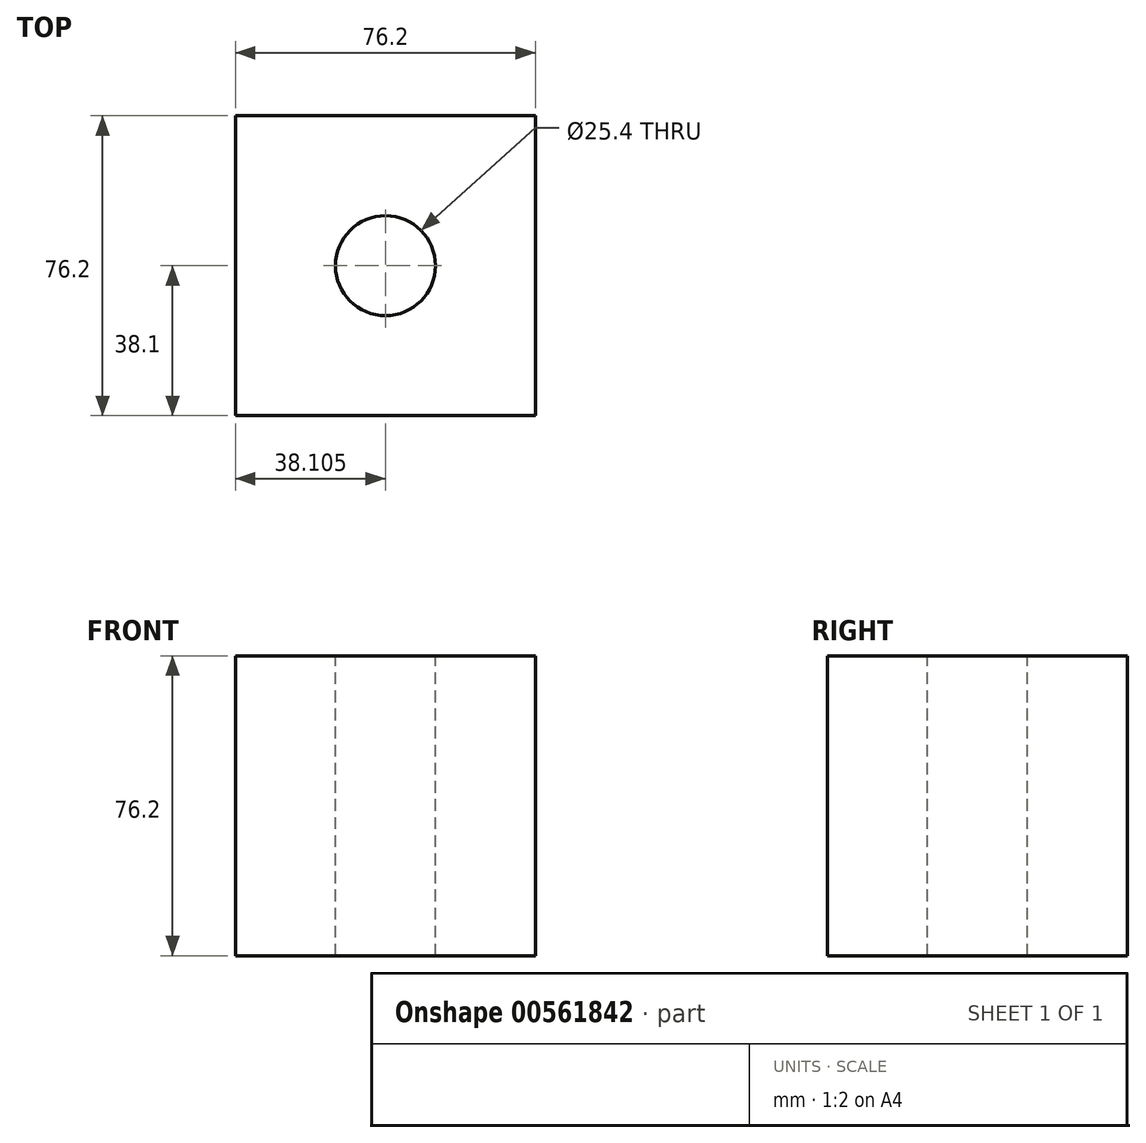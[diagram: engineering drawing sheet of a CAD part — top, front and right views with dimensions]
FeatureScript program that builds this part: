
annotation { "Feature Type Name" : "Feature", "Feature Type Description" : "" }
export const myFeature = defineFeature(function(context is Context, id is Id, definition is map)
    precondition{}
    {
        {
            var Q0;
            Q0=qCreatedBy(makeId("Front.planeOp"),FACE);
            var sketch = newSketch(context, id + "F0", { "sketchPlane" : qUnion([Q0])});
            skLineSegment(sketch, "E0.bottom", {"start": v(-44.93, 63.44) * mm, "end": v(31.27, 63.44) * mm});
            skLineSegment(sketch, "E0.top", {"start": v(-44.93, -12.76) * mm, "end": v(31.27, -12.76) * mm});
            skLineSegment(sketch, "E0.left", {"start": v(-44.93, 63.44) * mm, "end": v(-44.93, -12.76) * mm});
            skLineSegment(sketch, "E0.right", {"start": v(31.27, 63.44) * mm, "end": v(31.27, -12.76) * mm});
            skSolve(sketch);
        }
        {
            var Q0;
            Q0=makeQuery(id+"F0.imprint","IMPRINT",FACE,{"disambiguationData":[TD([[makeQuery(id+"F0.imprint","IMPRINT",EDGE,{"derivedFrom":sQuery(id+"F0.wireOp",EDGE,"E0.bottom")}),-1.0]])]});
            extrude(context, id + "F1", {"entities" : qUnion([Q0]), "depth" : 76.2 * mm, "offsetDistance" : 25.4 * mm});
        }
        {
            var Q0;
            Q0=makeQuery(id+"F1.opExtrude","SWEPT_FACE",FACE,{"disambiguationData":[OSD([sQuery(id+"F0.wireOp",EDGE,"E0.bottom")])]});
            var sketch = newSketch(context, id + "F2", { "sketchPlane" : qUnion([Q0])});
            skPoint(sketch, "E1", {"position": v(-6.83, -38.1) * mm});
            skSolve(sketch);
        }
        {
            var Q0;
            Q0=sQuery(id+"F2.wireOp",VERTEX,"E1");
            var Q1;
            Q1=makeQuery(id+"F1.opExtrude","SWEPT_BODY",BODY,{"disambiguationData":[OSD([sQuery(id+"F0.wireOp",EDGE,"E0.bottom"),sQuery(id+"F0.wireOp",EDGE,"E0.top"),sQuery(id+"F0.wireOp",EDGE,"E0.left"),sQuery(id+"F0.wireOp",EDGE,"E0.right")])]});
            hole(context, id + "F3", {"style" : HoleStyle.SIMPLE, "endStyle" : HoleEndStyle.THROUGH, "holeDiameter" : 25.4 * mm, "isTappedThrough" : true, "tappedDepth" : 12.7 * mm, "tapClearance" : 3, "locations" : qUnion([Q0]), "scope" : qUnion([Q1])});
        }
    });
